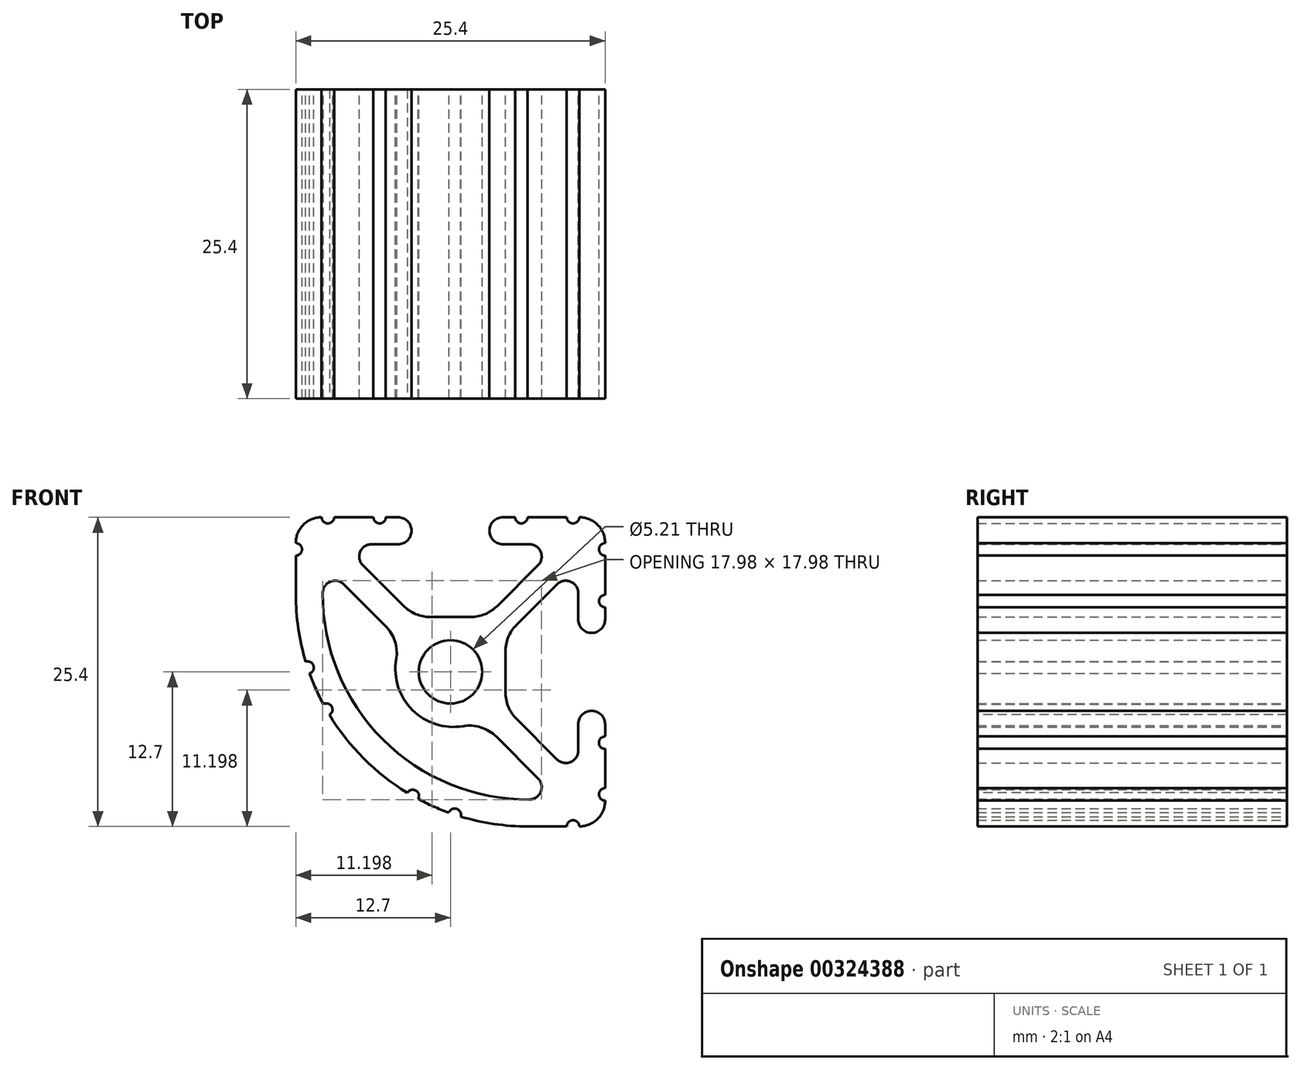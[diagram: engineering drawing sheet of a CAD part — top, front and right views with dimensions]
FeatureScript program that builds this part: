
annotation { "Feature Type Name" : "Feature", "Feature Type Description" : "" }
export const myFeature = defineFeature(function(context is Context, id is Id, definition is map)
    precondition{}
    {
        {
            var Q0;
            Q0=qCreatedBy(makeId("Front.planeOp"),FACE);
            var sketch = newSketch(context, id + "F0", { "sketchPlane" : qUnion([Q0])});
            skArc(sketch, "E0", {"start": v(-8.76, 7.2) * mm, "mid": v(-9.86, 7.41) * mm, "end": v(-10.49, 6.48) * mm});
            skLineSegment(sketch, "E1", {"start": v(-5.34, 3.78) * mm, "end": v(-8.76, 7.2) * mm});
            skArc(sketch, "E2", {"start": v(-4.46, 1.01) * mm, "mid": v(-4.56, 2.5) * mm, "end": v(-5.34, 3.78) * mm});
            skArc(sketch, "E3", {"start": v(-4.46, 1.01) * mm, "mid": v(-3.13, -3.13) * mm, "end": v(1.01, -4.46) * mm});
            skArc(sketch, "E4", {"start": v(3.78, -5.34) * mm, "mid": v(2.5, -4.56) * mm, "end": v(1.01, -4.46) * mm});
            skLineSegment(sketch, "E5", {"start": v(7.2, -8.76) * mm, "end": v(3.78, -5.34) * mm});
            skArc(sketch, "E6", {"start": v(6.48, -10.49) * mm, "mid": v(7.41, -9.86) * mm, "end": v(7.2, -8.76) * mm});
            skArc(sketch, "E7", {"start": v(-10.49, 6.48) * mm, "mid": v(-5.56, -5.56) * mm, "end": v(6.48, -10.49) * mm});
            skCircle(sketch, "E8", {"center": v(0, 0) * mm, "radius": 2.6 * mm});
            skArc(sketch, "E9", {"start": v(-12.7, 9.55) * mm, "mid": v(-12.2, 10.06) * mm, "end": v(-12.7, 10.58) * mm});
            skLineSegment(sketch, "E10", {"start": v(-12.7, 9.55) * mm, "end": v(-12.7, 6.35) * mm});
            skArc(sketch, "E11", {"start": v(-12.7, 6.35) * mm, "mid": v(-12.5, 3.57) * mm, "end": v(-11.89, 0.84) * mm});
            skArc(sketch, "E12", {"start": v(-11.57, -0.12) * mm, "mid": v(-11.25, 0.52) * mm, "end": v(-11.89, 0.84) * mm});
            skArc(sketch, "E13", {"start": v(-11.57, -0.12) * mm, "mid": v(-11.05, -1.4) * mm, "end": v(-10.44, -2.65) * mm});
            skArc(sketch, "E14", {"start": v(-9.94, -3.53) * mm, "mid": v(-9.75, -2.84) * mm, "end": v(-10.44, -2.65) * mm});
            skArc(sketch, "E15", {"start": v(-9.94, -3.53) * mm, "mid": v(-7.12, -7.12) * mm, "end": v(-3.53, -9.94) * mm});
            skArc(sketch, "E16", {"start": v(-2.65, -10.44) * mm, "mid": v(-2.84, -9.75) * mm, "end": v(-3.53, -9.94) * mm});
            skArc(sketch, "E17", {"start": v(-2.65, -10.44) * mm, "mid": v(-1.4, -11.05) * mm, "end": v(-0.12, -11.57) * mm});
            skArc(sketch, "E18", {"start": v(0.84, -11.89) * mm, "mid": v(0.52, -11.25) * mm, "end": v(-0.12, -11.57) * mm});
            skArc(sketch, "E19", {"start": v(0.84, -11.89) * mm, "mid": v(3.57, -12.5) * mm, "end": v(6.35, -12.7) * mm});
            skLineSegment(sketch, "E20", {"start": v(6.35, -12.7) * mm, "end": v(9.55, -12.7) * mm});
            skArc(sketch, "E21", {"start": v(10.58, -12.7) * mm, "mid": v(10.06, -12.2) * mm, "end": v(9.55, -12.7) * mm});
            skArc(sketch, "E22", {"start": v(10.58, -12.7) * mm, "mid": v(12.08, -12.08) * mm, "end": v(12.7, -10.58) * mm});
            skArc(sketch, "E23", {"start": v(12.7, -9.55) * mm, "mid": v(12.2, -10.06) * mm, "end": v(12.7, -10.58) * mm});
            skLineSegment(sketch, "E24", {"start": v(12.7, -9.55) * mm, "end": v(12.7, -6.32) * mm});
            skArc(sketch, "E25", {"start": v(12.7, -5.3) * mm, "mid": v(12.2, -5.82) * mm, "end": v(12.7, -6.32) * mm});
            skLineSegment(sketch, "E26", {"start": v(12.7, -5.3) * mm, "end": v(12.7, -4.3) * mm});
            skArc(sketch, "E27", {"start": v(12.7, -4.3) * mm, "mid": v(11.6, -3.2) * mm, "end": v(10.5, -4.3) * mm});
            skLineSegment(sketch, "E28", {"start": v(10.5, -4.3) * mm, "end": v(10.5, -6.47) * mm});
            skArc(sketch, "E29", {"start": v(8.76, -7.2) * mm, "mid": v(9.86, -7.41) * mm, "end": v(10.5, -6.47) * mm});
            skLineSegment(sketch, "E30", {"start": v(8.76, -7.2) * mm, "end": v(5.44, -3.88) * mm});
            skArc(sketch, "E31", {"start": v(4.5, -1.63) * mm, "mid": v(4.75, -2.85) * mm, "end": v(5.44, -3.88) * mm});
            skLineSegment(sketch, "E32", {"start": v(4.5, -1.63) * mm, "end": v(4.5, 1.63) * mm});
            skArc(sketch, "E33", {"start": v(5.44, 3.88) * mm, "mid": v(4.75, 2.85) * mm, "end": v(4.5, 1.63) * mm});
            skLineSegment(sketch, "E34", {"start": v(5.44, 3.88) * mm, "end": v(8.76, 7.2) * mm});
            skArc(sketch, "E35", {"start": v(10.5, 6.47) * mm, "mid": v(9.86, 7.41) * mm, "end": v(8.76, 7.2) * mm});
            skLineSegment(sketch, "E36", {"start": v(10.5, 6.47) * mm, "end": v(10.5, 4.3) * mm});
            skArc(sketch, "E37", {"start": v(10.5, 4.3) * mm, "mid": v(11.6, 3.2) * mm, "end": v(12.7, 4.3) * mm});
            skLineSegment(sketch, "E38", {"start": v(12.7, 4.3) * mm, "end": v(12.7, 5.3) * mm});
            skArc(sketch, "E39", {"start": v(12.7, 6.32) * mm, "mid": v(12.2, 5.82) * mm, "end": v(12.7, 5.3) * mm});
            skLineSegment(sketch, "E40", {"start": v(12.7, 6.32) * mm, "end": v(12.7, 9.55) * mm});
            skArc(sketch, "E41", {"start": v(12.7, 10.58) * mm, "mid": v(12.2, 10.06) * mm, "end": v(12.7, 9.55) * mm});
            skArc(sketch, "E42", {"start": v(12.7, 10.58) * mm, "mid": v(12.08, 12.08) * mm, "end": v(10.58, 12.7) * mm});
            skArc(sketch, "E43", {"start": v(9.55, 12.7) * mm, "mid": v(10.06, 12.2) * mm, "end": v(10.58, 12.7) * mm});
            skLineSegment(sketch, "E44", {"start": v(9.55, 12.7) * mm, "end": v(6.32, 12.7) * mm});
            skArc(sketch, "E45", {"start": v(5.3, 12.7) * mm, "mid": v(5.82, 12.2) * mm, "end": v(6.32, 12.7) * mm});
            skLineSegment(sketch, "E46", {"start": v(5.3, 12.7) * mm, "end": v(4.3, 12.7) * mm});
            skArc(sketch, "E47", {"start": v(4.3, 12.7) * mm, "mid": v(3.2, 11.6) * mm, "end": v(4.3, 10.5) * mm});
            skLineSegment(sketch, "E48", {"start": v(4.3, 10.5) * mm, "end": v(6.47, 10.5) * mm});
            skArc(sketch, "E49", {"start": v(7.2, 8.76) * mm, "mid": v(7.41, 9.86) * mm, "end": v(6.47, 10.5) * mm});
            skLineSegment(sketch, "E50", {"start": v(7.2, 8.76) * mm, "end": v(3.88, 5.44) * mm});
            skArc(sketch, "E51", {"start": v(1.63, 4.5) * mm, "mid": v(2.85, 4.75) * mm, "end": v(3.88, 5.44) * mm});
            skLineSegment(sketch, "E52", {"start": v(1.63, 4.5) * mm, "end": v(-1.63, 4.5) * mm});
            skArc(sketch, "E53", {"start": v(-3.88, 5.44) * mm, "mid": v(-2.85, 4.75) * mm, "end": v(-1.63, 4.5) * mm});
            skLineSegment(sketch, "E54", {"start": v(-3.88, 5.44) * mm, "end": v(-7.2, 8.76) * mm});
            skArc(sketch, "E55", {"start": v(-6.47, 10.5) * mm, "mid": v(-7.41, 9.86) * mm, "end": v(-7.2, 8.76) * mm});
            skLineSegment(sketch, "E56", {"start": v(-6.47, 10.5) * mm, "end": v(-4.3, 10.5) * mm});
            skArc(sketch, "E57", {"start": v(-4.3, 10.5) * mm, "mid": v(-3.2, 11.6) * mm, "end": v(-4.3, 12.7) * mm});
            skLineSegment(sketch, "E58", {"start": v(-4.3, 12.7) * mm, "end": v(-5.3, 12.7) * mm});
            skArc(sketch, "E59", {"start": v(-6.32, 12.7) * mm, "mid": v(-5.82, 12.2) * mm, "end": v(-5.3, 12.7) * mm});
            skLineSegment(sketch, "E60", {"start": v(-6.32, 12.7) * mm, "end": v(-9.55, 12.7) * mm});
            skArc(sketch, "E61", {"start": v(-10.58, 12.7) * mm, "mid": v(-10.06, 12.2) * mm, "end": v(-9.55, 12.7) * mm});
            skArc(sketch, "E62", {"start": v(-10.58, 12.7) * mm, "mid": v(-12.08, 12.08) * mm, "end": v(-12.7, 10.58) * mm});
            skSolve(sketch);
        }
        {
            var Q0;
            Q0=makeQuery(id+"F0.imprint","IMPRINT",FACE,{"disambiguationData":[TD([[makeQuery(id+"F0.imprint","IMPRINT",EDGE,{"derivedFrom":sQuery(id+"F0.wireOp",EDGE,"E0")}),-1.0]])]});
            extrude(context, id + "F1", {"entities" : qUnion([Q0]), "depth" : 25.4 * mm});
        }
    });
